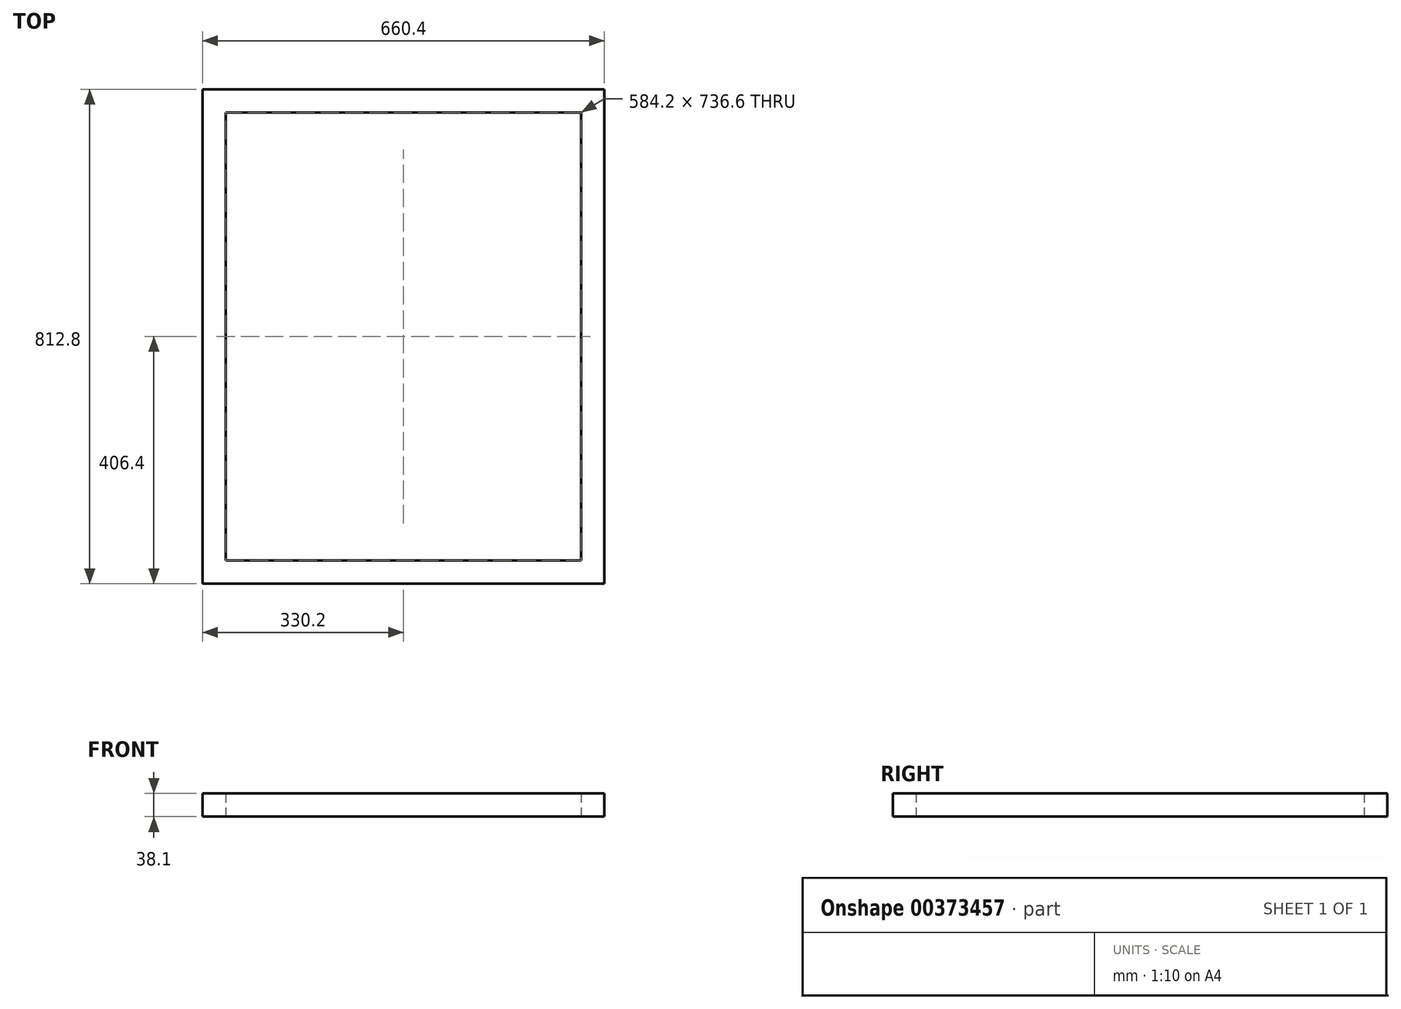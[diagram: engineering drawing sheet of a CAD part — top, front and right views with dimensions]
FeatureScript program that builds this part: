
annotation { "Feature Type Name" : "Feature", "Feature Type Description" : "" }
export const myFeature = defineFeature(function(context is Context, id is Id, definition is map)
    precondition{}
    {
        {
            var Q0;
            Q0=qCreatedBy(makeId("Top.planeOp"),FACE);
            var sketch = newSketch(context, id + "F0", { "sketchPlane" : qUnion([Q0])});
            skLineSegment(sketch, "E0.bottom", {"start": v(330.2, -406.4) * mm, "end": v(-330.2, -406.4) * mm});
            skLineSegment(sketch, "E0.top", {"start": v(330.2, 406.4) * mm, "end": v(-330.2, 406.4) * mm});
            skLineSegment(sketch, "E0.left", {"start": v(330.2, -406.4) * mm, "end": v(330.2, 406.4) * mm});
            skLineSegment(sketch, "E0.right", {"start": v(-330.2, -406.4) * mm, "end": v(-330.2, 406.4) * mm});
            skPoint(sketch, "E0.middle", {"position": v(0, 0) * mm});
            skLineSegment(sketch, "E1.bottom", {"start": v(292.1, 368.3) * mm, "end": v(-292.1, 368.3) * mm});
            skLineSegment(sketch, "E1.top", {"start": v(292.1, -368.3) * mm, "end": v(-292.1, -368.3) * mm});
            skLineSegment(sketch, "E1.left", {"start": v(292.1, 368.3) * mm, "end": v(292.1, -368.3) * mm});
            skLineSegment(sketch, "E1.right", {"start": v(-292.1, 368.3) * mm, "end": v(-292.1, -368.3) * mm});
            skSolve(sketch);
        }
        {
            var Q0;
            Q0 = qSketchRegion(id + "F0", true);
            extrude(context, id + "F1", {"entities" : qUnion([Q0]), "depth" : 38.1 * mm});
        }
    });
